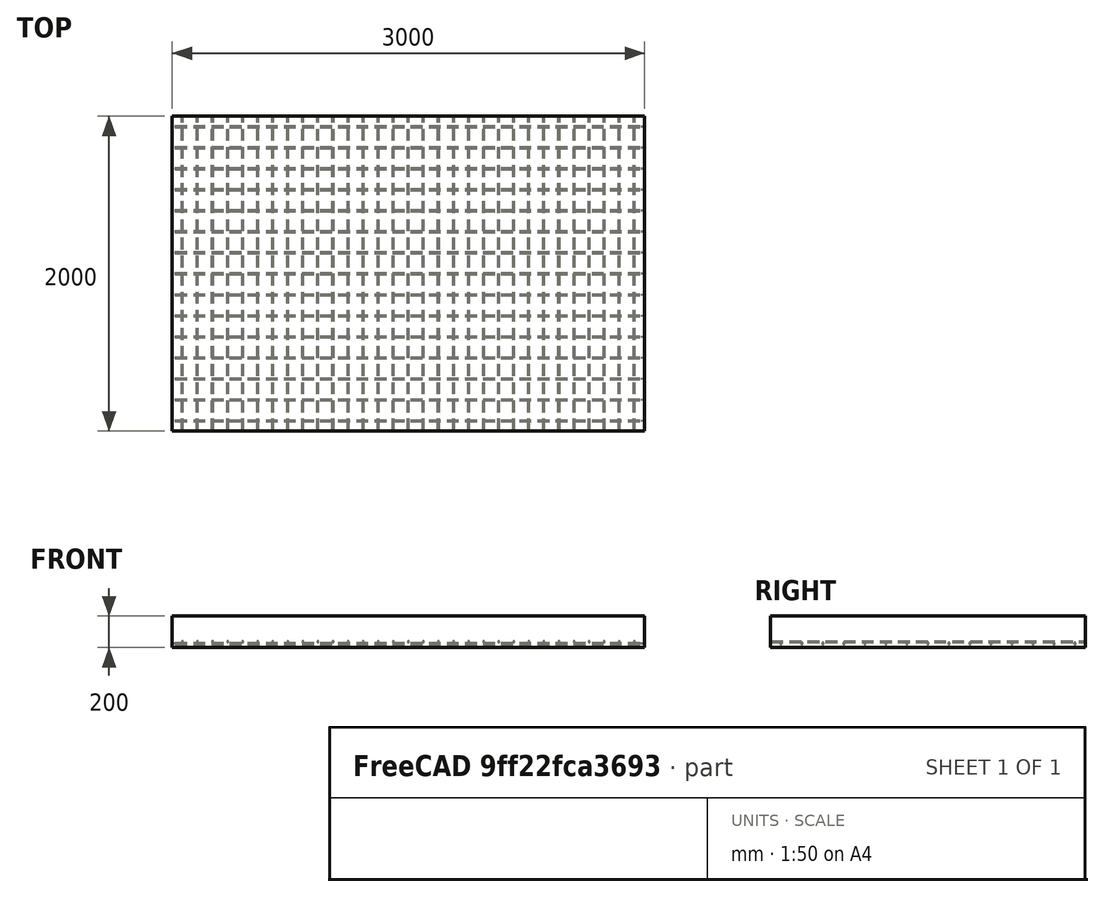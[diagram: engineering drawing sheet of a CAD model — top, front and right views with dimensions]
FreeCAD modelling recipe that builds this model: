
FCSTD DOCUMENT  (FreeCAD 0.21R33771 (Git))
Label: 3D Designe of Rainforced Slab
License: All rights reserved
objects: Part::FeaturePython×3, Sketcher::SketchObject×2
note: 5 computed .brp shape members not serialized (recipe doc carries the construction recipe); baked Part::Feature solids carry a one-line shape summary decoded from their .brp

FEATURE [Part::FeaturePython] Structure  label="Slab"  # Arch/BIM 118 (typed FeaturePython)
  BaseMirror = false
  BaseOffsetX = 0
  BaseOffsetY = 0
  BasePerpendicularToTool = false
  BaseRotation = 0
  ComputedLength = 200
  FaceMaker = 0
  Height = 200
  HorizontalArea = 6000000
  IfcData = attributes={"GlobalId": {"name": "GlobalId", "type": "IfcGloballyUniqueId", "is_enum": false, "enum_values": []}, "Description": {"... (+452 chars omitted),+1 more (map truncated)
  IfcType = 118
  Length = 3000
  MoveBase = false
  MoveWithHost = false
  Nodes = (4) [(-1500,-1000,0),(1500,-1000,0),(1500,1000,0),(-1500,1000,0)]
  NodesOffset = 0
  Normal = (0,0,0)
  PerimeterLength = 10000
  PredefinedType = 1
  ToolOffsetFirst = 0
  ToolOffsetLast = 0
  VerticalArea = 2000000
  Width = 2000
FEATURE [Sketcher::SketchObject] Sketch
  FullyConstrained = false
  MapMode = 5
  Placement = pos=(0,-1000,0) rot=(1,0,0;1.5708rad)
  Support = -> [Structure]
  sketch-geometry (1):
    g0: LineSegment StartX=-1480 StartY=26 StartZ=0 EndX=1480 EndY=26 EndZ=0
FEATURE [Part::FeaturePython] Rebar  label="StraightRebar"  # Arch/BIM 110 (typed FeaturePython)
  Amount = 15
  AmountCheck = false
  Base = -> Sketch
  Cover = 20
  CoverAlong = Bottom Side
  Diameter = 12
  Direction = (0,0,0)
  Distance = 0
  FrontCover = 60
  HorizontalArea = 0
  Host = -> Structure
  IfcType = 110
  LeftBottomCover = 20
  Length = 2960
  Mark = StraightRebar
  MoveBase = false
  MoveWithHost = false
  OffsetEnd = 66
  OffsetStart = 66
  Orientation = Horizontal
  PerimeterLength = 0
  PlacementList = 15 placements: arithmetic series from (0,66,-1.46549e-14) step (0,133.429,-2.96271e-14) to (0,1934,-4.29434e-13)
  RebarShape = 0
  RightTopCover = 20
  Rounding = 0
  Spacing = 133.429
  TotalLength = 44400
  TrueSpacing = 150
  VerticalArea = 0
FEATURE [Sketcher::SketchObject] Sketch001
  FullyConstrained = false
  MapMode = 5
  Placement = pos=(1500,0,0) rot=(0.57735,0.57735,0.57735;2.0944rad)
  Support = -> [Structure]
  sketch-geometry (1):
    g0: LineSegment StartX=-995 StartY=37 StartZ=0 EndX=995 EndY=37 EndZ=0
FEATURE [Part::FeaturePython] Rebar001  label="StraightRebar001"  # Arch/BIM 110 (typed FeaturePython)
  Amount = 31
  AmountCheck = false
  Base = -> Sketch001
  Cover = 32
  CoverAlong = Bottom Side
  Diameter = 10
  Direction = (0,0,0)
  Distance = 0
  FrontCover = 60
  HorizontalArea = 0
  Host = -> Structure
  IfcType = 110
  LeftBottomCover = 5
  Length = 1990
  Mark = StraightRebar001
  MoveBase = false
  MoveWithHost = false
  OffsetEnd = 65
  OffsetStart = 65
  Orientation = Horizontal
  PerimeterLength = 0
  PlacementList = 31 placements: arithmetic series from (-65,0,0) step (-95.6667,0,0) to (-2935,0,0)
  RebarShape = 0
  RightTopCover = 5
  Rounding = 0
  Spacing = 95.6667
  TotalLength = 61690
  TrueSpacing = 100
  VerticalArea = 0
